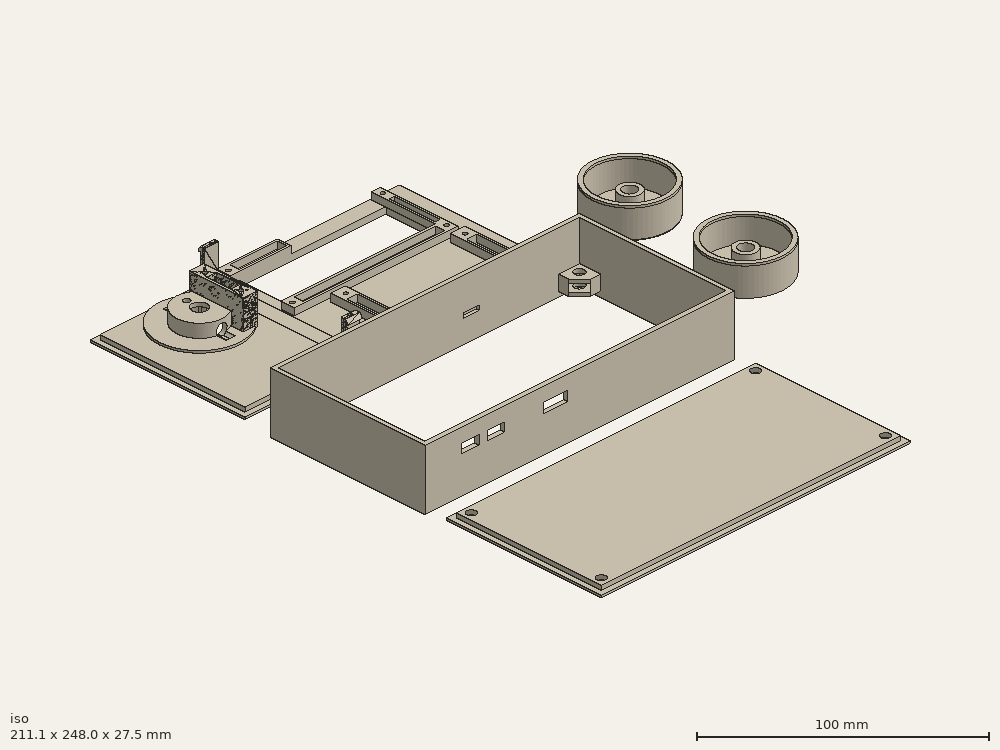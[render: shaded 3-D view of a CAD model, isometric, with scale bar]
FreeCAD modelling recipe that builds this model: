
FCSTD DOCUMENT  (FreeCAD 0.18.4R)
Label: controlbox
License: All rights reserved
LicenseURL: http://en.wikipedia.org/wiki/All_rights_reserved
objects: Part::Extrusion×22, Part::Feature×21, Part::Part2DObjectPython×20, Part::MultiFuse×20, Part::FeaturePython×12, Part::Cut×12, App::DocumentObjectGroup×6
note: 107 computed .brp shape members not serialized (recipe doc carries the construction recipe); baked Part::Feature solids carry a one-line shape summary decoded from their .brp

FEATURE [Part::Feature] Cut279012044
  Placement = pos=(203.269,1.91073,-1) rot=(0,0,1;0rad)
  shape: bbox 150 x 75.1 x 3 mm, 15 faces (baked)
FEATURE [App::DocumentObjectGroup] GrExplode_Slice  label="Exploded Slice"
FEATURE [App::DocumentObjectGroup] GrExplode_Slice001  label="Exploded Slice001"
FEATURE [App::DocumentObjectGroup] GrExplode_Slice002  label="Exploded Slice002"
FEATURE [Part::Part2DObjectPython] Rectangle006  # Draft 2D object (typed FeaturePython)
  ChamferSize = 0
  Columns = 1
  FilletRadius = 0
  Height = 73.0083
  Length = 53.7046
  MakeFace = true
  Placement = pos=(123.234,41.9071,-37.9227) rot=(0.57735,-0.57735,-0.57735;2.0944rad)
  Rows = 1
FEATURE [Part::FeaturePython] Slice003  # WARN: FeaturePython — macro-defined, semantics opaque (R4)
  Mode = 1
  Tolerance = 0
  Tools = -> [Rectangle006]
FEATURE [Part::FeaturePython] Slice003_child0  label="Slice003.0"  # WARN: FeaturePython — macro-defined, semantics opaque (R4)
  Base = -> Slice003
  FilterType = 1
  Invert = false
  OverrideMaxVal = 0
  WindowFrom = 80
  WindowTo = 100
  items = 0
FEATURE [Part::Feature] Face004
  shape: bbox 1.25 x 11.65 x 1.196e-06 mm, 1 faces, 0 solids (baked)
FEATURE [Part::Extrusion] Extrusion048
  Base = -> Face004
  Dir = (-1e-15,1e-16,-4)
  DirMode = 0
  FaceMakerClass = Part::FaceMakerBullseye
  LengthFwd = 0
  LengthRev = 0
  Solid = true
  Symmetric = false
FEATURE [Part::MultiFuse] Fusion
  Shapes = -> [Slice003_child0,Extrusion048]
FEATURE [App::DocumentObjectGroup] GrExplode_Slice003  label="Exploded Slice003"
  Group = -> [Fusion]
FEATURE [Part::Feature] Fusion016003002002002002003007002002020008005003005004002003002008
  shape: bbox 7 x 26 x 14.5 mm, 14 faces (baked)
FEATURE [Part::Feature] Cut279012081006007001  label="Cut279012081006008"
  shape: bbox 22 x 22 x 7 mm, 8 faces (baked)
FEATURE [Part::Part2DObjectPython] Circle022  # Draft 2D object (typed FeaturePython)
  FirstAngle = 0
  LastAngle = 0
  MakeFace = true
  Placement = pos=(117.234,41.9934,4.6) rot=(0,0.707107,0.707107;3.14159rad)
  Radius = 2.6
FEATURE [Part::Extrusion] Extrusion049
  Base = -> Circle022
  Dir = (0,-69.8017,1.55e-14)
  DirMode = 0
  FaceMakerClass = Part::FaceMakerBullseye
  LengthFwd = 0
  LengthRev = 0
  Solid = true
  Symmetric = false
FEATURE [Part::Part2DObjectPython] Circle023  # Draft 2D object (typed FeaturePython)
  FirstAngle = 0
  LastAngle = 0
  MakeFace = true
  Placement = pos=(117.234,22.5909,2) rot=(0,0,1;0rad)
  Radius = 18.3
FEATURE [Part::Part2DObjectPython] Circle024  # Draft 2D object (typed FeaturePython)
  FirstAngle = 0
  LastAngle = 0
  MakeFace = true
  Placement = pos=(117.234,22.5909,2) rot=(1,0,0;3.14159rad)
  Radius = 8
FEATURE [Part::Extrusion] Extrusion050
  Base = -> Circle024
  Dir = (-4.2e-15,-8.8e-15,-36)
  DirMode = 0
  FaceMakerClass = Part::FaceMakerBullseye
  LengthFwd = 0
  LengthRev = 0
  Solid = true
  Symmetric = false
FEATURE [Part::Extrusion] Extrusion051
  Base = -> Circle023
  Dir = (-1e-16,-2e-16,-1)
  DirMode = 0
  FaceMakerClass = Part::FaceMakerBullseye
  LengthFwd = 0
  LengthRev = 0
  Solid = true
  Symmetric = false
FEATURE [Part::Cut] Cut279012081006007003
  Base = -> Extrusion051
  Tool = -> Extrusion050
FEATURE [Part::Cut] Cut279012081006007004
  Base = -> Cut279012081006007001
  Tool = -> Extrusion049
FEATURE [Part::Part2DObjectPython] Circle027  # Draft 2D object (typed FeaturePython)
  FirstAngle = 0
  LastAngle = 0
  MakeFace = true
  Placement = pos=(117.234,22.5909,6) rot=(1,0,0;3.14159rad)
  Radius = 8
  Support = -> [Cut279012081006007004]
FEATURE [Part::Extrusion] Extrusion052
  Base = -> Circle027
  Dir = (1e-16,3e-16,1.2)
  DirMode = 0
  FaceMakerClass = Part::FaceMakerBullseye
  LengthFwd = 0
  LengthRev = 0
  Solid = true
  Symmetric = false
FEATURE [Part::Cut] Cut279012081006007005
  Base = -> Cut279012081006007004
  Tool = -> Extrusion052
FEATURE [Part::Feature] Cut279012081002001  label="Cut279012081006007006"
  shape: bbox 38.81 x 38.81 x 1 mm, 4 faces (baked)
FEATURE [Part::Part2DObjectPython] Circle  # Draft 2D object (typed FeaturePython)
  FirstAngle = 0
  LastAngle = 0
  MakeFace = true
  Placement = pos=(117.217,37.7921,4.5999) rot=(-1,0,0;1.5708rad)
  Radius = 2.7
  Support = -> [Cut279012081002001]
FEATURE [Part::Extrusion] Extrusion053
  Base = -> Circle
  Dir = (-1.9e-15,-30.4017,6.8e-15)
  DirMode = 0
  FaceMakerClass = Part::FaceMakerBullseye
  LengthFwd = 0
  LengthRev = 0
  Solid = true
  Symmetric = false
FEATURE [Part::Cut] Cut279012081006007006  label="Cut279012081006007007"
  Base = -> Cut279012081002001
  Tool = -> Extrusion053
FEATURE [Part::MultiFuse] Fusion016003002002002002003007002002020008005003005004002003002010
  Shapes = -> [Cut279012081006007005,Cut279012081006007006]
FEATURE [Part::MultiFuse] Fusion016003002002002002003007002002020008005003005004002003002011
  Shapes = -> [Fusion016003002002002002003007002002020008005003005004002003002010,Fusion016003002002002002003007002002020008005003005004002003002008]
FEATURE [Part::MultiFuse] Fusion016003002002002002003007002002020008005003005004002003002012
  Shapes = -> [Cut279012081006007003,Fusion016003002002002002003007002002020008005003005004002003002011]
FEATURE [Part::Feature] Cut279012081006003001  label="Cut279012081006007008"
  shape: bbox 150 x 75.1 x 6.5 mm, 76 faces (baked)
FEATURE [Part::MultiFuse] Fusion016003002002002002003007002002020008005003005004002003002013
  Shapes = -> [Cut279012081006003001,Fusion016003002002002002003007002002020008005003005004002003002012]
FEATURE [Part::Feature] Fusion016003002002002002003007002002020008005003005004002003002014001  label="Fusion016003002002002002003007002002020008005003005004002003002015"
  shape: bbox 7 x 4.25 x 15 mm, 9 faces (baked)
FEATURE [Part::MultiFuse] Fusion016003002002002002003007002002020008005003005004002003002014002
  Shapes = -> [Fusion016003002002002002003007002002020008005003005004002003002013,Fusion016003002002002002003007002002020008005003005004002003002014001]
FEATURE [Part::Feature] Fusion016003002002002002003007002002020008005003005004002003002014004001  label="Fusion016003002002002002003007002002020008005003005004002003002014005"
  shape: bbox 7 x 4.25 x 15 mm, 9 faces (baked)
FEATURE [Part::MultiFuse] Fusion016003002002002002003007002002020008005003005004002003002014004002
  Shapes = -> [Fusion016003002002002002003007002002020008005003005004002003002014002,Fusion016003002002002002003007002002020008005003005004002003002014004001]
FEATURE [Part::Feature] Face
  shape: bbox 7 x 2e-07 x 13 mm, 1 faces, 0 solids (baked)
FEATURE [Part::Extrusion] Extrusion061
  Base = -> Face
  Dir = (0,1,0)
  DirMode = 0
  FaceMakerClass = Part::FaceMakerBullseye
  LengthFwd = 0
  LengthRev = 0
  Solid = true
  Symmetric = false
FEATURE [Part::Feature] Face005
  shape: bbox 7 x 1 x 4.243e-07 mm, 1 faces, 0 solids (baked)
FEATURE [Part::Extrusion] Extrusion062
  Base = -> Face005
  Dir = (0,0,-2)
  DirMode = 0
  FaceMakerClass = Part::FaceMakerBullseye
  LengthFwd = 0
  LengthRev = 0
  Solid = true
  Symmetric = false
FEATURE [Part::MultiFuse] Fusion016003002002002002003007002002020008005003005004002003002014004003
  Shapes = -> [Extrusion061,Extrusion062]
FEATURE [Part::Part2DObjectPython] Rectangle012  # Draft 2D object (typed FeaturePython)
  ChamferSize = 0
  Columns = 1
  FilletRadius = 0
  Height = 3
  Length = 3
  MakeFace = true
  Placement = pos=(136.979,-23.4591,2) rot=(0.57735,-0.57735,-0.57735;2.0944rad)
  Rows = 1
FEATURE [Part::Part2DObjectPython] Circle030  # Draft 2D object (typed FeaturePython)
  FirstAngle = 0
  LastAngle = 0
  MakeFace = true
  Placement = pos=(136.979,-23.4591,5) rot=(0.57735,-0.57735,-0.57735;2.0944rad)
  Radius = 3
FEATURE [Part::Extrusion] Extrusion063
  Base = -> Rectangle012
  Dir = (7,0,0)
  DirMode = 0
  FaceMakerClass = Part::FaceMakerBullseye
  LengthFwd = 0
  LengthRev = 0
  Solid = true
  Symmetric = false
FEATURE [Part::Extrusion] Extrusion064
  Base = -> Circle030
  Dir = (7,0,0)
  DirMode = 0
  FaceMakerClass = Part::FaceMakerBullseye
  LengthFwd = 0
  LengthRev = 0
  Solid = true
  Symmetric = false
FEATURE [Part::Cut] Cut279012081006007008  label="Cut279012081006007010"
  Base = -> Extrusion063
  Tool = -> Extrusion064
FEATURE [Part::MultiFuse] Fusion016003002002002002003007002002020008005003005004002003002014004004
  Shapes = -> [Fusion016003002002002002003007002002020008005003005004002003002014004003,Cut279012081006007008]
FEATURE [Part::MultiFuse] Fusion016003002002002002003007002002020008005003005004002003002014004005
  Shapes = -> [Fusion016003002002002002003007002002020008005003005004002003002014004002,Fusion016003002002002002003007002002020008005003005004002003002014004004]
FEATURE [Part::Feature] Face006
  shape: bbox 7 x 2e-07 x 13 mm, 1 faces, 0 solids (baked)
FEATURE [Part::Extrusion] Extrusion065
  Base = -> Face006
  Dir = (0,-1,0)
  DirMode = 0
  FaceMakerClass = Part::FaceMakerBullseye
  LengthFwd = 0
  LengthRev = 0
  Solid = true
  Symmetric = false
FEATURE [Part::Feature] Face007
  shape: bbox 7 x 1 x 4.243e-07 mm, 1 faces, 0 solids (baked)
FEATURE [Part::Extrusion] Extrusion066
  Base = -> Face007
  Dir = (0,0,-2)
  DirMode = 0
  FaceMakerClass = Part::FaceMakerBullseye
  LengthFwd = 0
  LengthRev = 0
  Solid = true
  Symmetric = false
FEATURE [Part::Part2DObjectPython] Rectangle013  # Draft 2D object (typed FeaturePython)
  ChamferSize = 0
  Columns = 1
  FilletRadius = 0
  Height = 3
  Length = 3
  MakeFace = true
  Placement = pos=(136.979,39.9935,2) rot=(0.57735,-0.57735,-0.57735;2.0944rad)
  Rows = 1
  Support = -> [Extrusion066]
FEATURE [Part::Part2DObjectPython] Circle031  # Draft 2D object (typed FeaturePython)
  FirstAngle = 0
  LastAngle = 0
  MakeFace = true
  Placement = pos=(136.979,36.9935,5) rot=(0.57735,-0.57735,-0.57735;2.0944rad)
  Radius = 3
  Support = -> [Extrusion065]
FEATURE [Part::Extrusion] Extrusion067
  Base = -> Rectangle013
  Dir = (7,0,0)
  DirMode = 0
  FaceMakerClass = Part::FaceMakerBullseye
  LengthFwd = 0
  LengthRev = 0
  Solid = true
  Symmetric = false
FEATURE [Part::Extrusion] Extrusion068
  Base = -> Circle031
  Dir = (7,0,0)
  DirMode = 0
  FaceMakerClass = Part::FaceMakerBullseye
  LengthFwd = 0
  LengthRev = 0
  Solid = true
  Symmetric = false
FEATURE [Part::Cut] Cut279012081006007009  label="Cut279012081006007011"
  Base = -> Extrusion067
  Tool = -> Extrusion068
FEATURE [Part::MultiFuse] Fusion016003002002002002003007002002020008005003005004002003002014004006
  Shapes = -> [Cut279012081006007009,Extrusion065]
FEATURE [Part::MultiFuse] Fusion016003002002002002003007002002020008005003005004002003002014004007
  Shapes = -> [Fusion016003002002002002003007002002020008005003005004002003002014004005,Fusion016003002002002002003007002002020008005003005004002003002014004006]
FEATURE [Part::MultiFuse] Fusion016003002002002002003007002002020008005003005004002003002014004008
  Shapes = -> [Fusion016003002002002002003007002002020008005003005004002003002014004007,Extrusion066]
FEATURE [Part::Part2DObjectPython] Rectangle014  # Draft 2D object (typed FeaturePython)
  ChamferSize = 0
  Columns = 1
  FilletRadius = 0
  Height = 70.4526
  Length = 7
  MakeFace = true
  Placement = pos=(136.979,-28.4591,2) rot=(0,0,1;0rad)
  Rows = 1
  Support = -> [Fusion016003002002002002003007002002020008005003005004002003002014004008]
FEATURE [Part::FeaturePython] Slice  # WARN: FeaturePython — macro-defined, semantics opaque (R4)
  Base = -> Fusion016003002002002002003007002002020008005003005004002003002014004008
  Mode = 1
  Tolerance = 0
  Tools = -> [Rectangle014]
FEATURE [Part::FeaturePython] Slice_child0  label="Slice.0"  # WARN: FeaturePython — macro-defined, semantics opaque (R4)
  Base = -> Slice
  FilterType = 1
  Invert = false
  OverrideMaxVal = 0
  WindowFrom = 80
  WindowTo = 100
  items = 0
FEATURE [Part::FeaturePython] Slice_child1001  label="Slice.002"  # WARN: FeaturePython — macro-defined, semantics opaque (R4)
  Base = -> Slice
  FilterType = 1
  Invert = false
  OverrideMaxVal = 0
  WindowFrom = 80
  WindowTo = 100
  items = 1
FEATURE [Part::FeaturePython] Slice_child2  label="Slice.2"  # WARN: FeaturePython — macro-defined, semantics opaque (R4)
  Base = -> Slice
  FilterType = 1
  Invert = false
  OverrideMaxVal = 0
  WindowFrom = 80
  WindowTo = 100
  items = 2
FEATURE [Part::FeaturePython] Slice_child3  label="Slice.3"  # WARN: FeaturePython — macro-defined, semantics opaque (R4)
  Base = -> Slice
  FilterType = 1
  Invert = false
  OverrideMaxVal = 0
  WindowFrom = 80
  WindowTo = 100
  items = 3
FEATURE [Part::FeaturePython] Slice_child4  label="Slice.4"  # WARN: FeaturePython — macro-defined, semantics opaque (R4)
  Base = -> Slice
  FilterType = 1
  Invert = false
  OverrideMaxVal = 0
  WindowFrom = 80
  WindowTo = 100
  items = 4
FEATURE [Part::Feature] Slice_child3001  label="Slice.003"
  shape: bbox 7 x 6.25 x 15 mm, 9 faces (baked)
FEATURE [Part::Feature] Slice_child0001  label="Slice.004"
  shape: bbox 7 x 6.25 x 15 mm, 9 faces (baked)
FEATURE [Part::MultiFuse] Fusion016003002002002002003007002002020008005003005004002003002014004009
  Shapes = -> [Slice_child3001,Slice_child0001]
FEATURE [Part::MultiFuse] Fusion016003002002002002003007002002020008005003005004002003002014004010
  Shapes = -> [Slice_child2,Fusion016003002002002002003007002002020008005003005004002003002014004009]
FEATURE [Part::Part2DObjectPython] Line  # Draft 2D object (typed FeaturePython)
  ChamferSize = 0
  Closed = false
  End = (297.043,-80.6345,11.8)
  FilletRadius = 0
  Length = 12.8
  MakeFace = true
  Placement = pos=(297.043,-80.6345,-1) rot=(0,0,1;0rad)
  Points = (2) [(0,0,0),(0,0,12.8)]
  Start = (297.043,-80.6345,-1)
  Subdivisions = 0
FEATURE [Part::Feature] Fusion016003002002002002003007002002020008005003005004002003002014004011001  label="Fusion016003002002002002003007002002020008005003005004002003002014004012"
  shape: bbox 36 x 36 x 12.8 mm, 11 faces (baked)
FEATURE [Part::Part2DObjectPython] Line001  # Draft 2D object (typed FeaturePython)
  ChamferSize = 0
  Closed = false
  End = (297.043,-24.3987,12.8)
  FilletRadius = 0
  Length = 13.8
  MakeFace = true
  Placement = pos=(297.043,-24.3987,-1) rot=(0,0,1;0rad)
  Points = (2) [(0,0,0),(0,0,13.8)]
  Start = (297.043,-24.3987,-1)
  Subdivisions = 0
FEATURE [Part::Feature] Fusion016003002002002002003007002002020008005003005004002003002014004011002001  label="Fusion016003002002002002003007002002020008005003005004002003002014004011003"
  shape: bbox 36 x 36 x 12.8 mm, 13 faces (baked)
FEATURE [Part::Part2DObjectPython] Rectangle017  # Draft 2D object (typed FeaturePython)
  ChamferSize = 0
  Columns = 1
  FilletRadius = 0
  Height = 70
  Length = 70
  MakeFace = true
  Placement = pos=(230.617,5.027,-0.7) rot=(1,0,0;3.14159rad)
  Rows = 1
  Support = -> [Fusion016003002002002002003007002002020008005003005004002003002014004011001]
FEATURE [Part::FeaturePython] Slice004  # WARN: FeaturePython — macro-defined, semantics opaque (R4)
  Base = -> Fusion016003002002002002003007002002020008005003005004002003002014004011002001
  Mode = 1
  Tolerance = 0
  Tools = -> [Rectangle017]
FEATURE [Part::FeaturePython] Slice004_child0  label="Slice004.0"  # WARN: FeaturePython — macro-defined, semantics opaque (R4)
  Base = -> Slice004
  FilterType = 1
  Invert = false
  OverrideMaxVal = 0
  WindowFrom = 80
  WindowTo = 100
  items = 0
FEATURE [Part::FeaturePython] Slice004_child1  label="Slice004.1"  # WARN: FeaturePython — macro-defined, semantics opaque (R4)
  Base = -> Slice004
  FilterType = 1
  Invert = false
  OverrideMaxVal = 0
  WindowFrom = 80
  WindowTo = 100
  items = 1
FEATURE [Part::FeaturePython] Slice004_child2  label="Slice004.2"  # WARN: FeaturePython — macro-defined, semantics opaque (R4)
  Base = -> Slice004
  FilterType = 1
  Invert = false
  OverrideMaxVal = 0
  WindowFrom = 80
  WindowTo = 100
  items = 2
FEATURE [Part::Part2DObjectPython] Circle032  # Draft 2D object (typed FeaturePython)
  FirstAngle = 0
  LastAngle = 0
  MakeFace = true
  Placement = pos=(279.043,-24.3987,-0.7) rot=(1,0,0;3.14159rad)
  Radius = 15
FEATURE [Part::Extrusion] Extrusion
  Base = -> Circle032
  Dir = (0,0,26.1259)
  DirMode = 0
  FaceMakerClass = Part::FaceMakerBullseye
  LengthFwd = 0
  LengthRev = 0
  Solid = true
  Symmetric = false
FEATURE [Part::Part2DObjectPython] Circle033  # Draft 2D object (typed FeaturePython)
  FirstAngle = 0
  LastAngle = 0
  MakeFace = true
  Placement = pos=(279.043,-24.3987,-0.7) rot=(1,0,0;3.14159rad)
  Radius = 16
  Support = -> [Slice004_child2]
FEATURE [Part::Extrusion] Extrusion069
  Base = -> Circle033
  Dir = (0,0,26.1259)
  DirMode = 0
  FaceMakerClass = Part::FaceMakerBullseye
  LengthFwd = 0
  LengthRev = 0
  Solid = true
  Symmetric = false
FEATURE [Part::Cut] Cut
  Base = -> Extrusion069
  Tool = -> Extrusion
FEATURE [Part::Cut] Cut279012081006007010  label="Cut279012081006007012"
  Base = -> Slice004_child2
  Tool = -> Cut
FEATURE [Part::Part2DObjectPython] Circle035  # Draft 2D object (typed FeaturePython)
  FirstAngle = 0
  LastAngle = 0
  MakeFace = true
  Placement = pos=(279.043,-24.3987,-0.7) rot=(1,0,0;3.14159rad)
  Radius = 15
  Support = -> [Cut279012081006007010]
FEATURE [Part::Extrusion] Extrusion071
  Base = -> Circle035
  Dir = (0,0,62.2869)
  DirMode = 0
  FaceMakerClass = Part::FaceMakerBullseye
  LengthFwd = 0
  LengthRev = 0
  Solid = true
  Symmetric = false
FEATURE [Part::Part2DObjectPython] Circle036  # Draft 2D object (typed FeaturePython)
  FirstAngle = 0
  LastAngle = 0
  MakeFace = true
  Placement = pos=(279.043,-24.3987,-0.7) rot=(1,0,0;3.14159rad)
  Radius = 14
  Support = -> [Cut279012081006007010]
FEATURE [Part::Extrusion] Extrusion072
  Base = -> Circle036
  Dir = (0,0,62.2869)
  DirMode = 0
  FaceMakerClass = Part::FaceMakerBullseye
  LengthFwd = 0
  LengthRev = 0
  Solid = true
  Symmetric = false
FEATURE [Part::Cut] Cut279012081006007011  label="Cut279012081006007013"
  Base = -> Extrusion071
  Tool = -> Extrusion072
FEATURE [Part::Cut] Cut279012081006007012  label="Cut279012081006007014"
  Base = -> Cut279012081006007010
  Tool = -> Cut279012081006007011
FEATURE [Part::MultiFuse] Fusion016003002002002002003007002002020008005003005004002003002014004011002002
  Shapes = -> [Slice004_child1,Slice004_child0]
FEATURE [Part::MultiFuse] Fusion016003002002002002003007002002020008005003005004002003002014004011002003
  Shapes = -> [Cut279012081006007012,Fusion016003002002002002003007002002020008005003005004002003002014004011002002]
FEATURE [Part::Feature] Face008
  shape: bbox 1.25 x 10.58 x 1.691e-06 mm, 1 faces, 0 solids (baked)
FEATURE [Part::Extrusion] Extrusion073
  Base = -> Face008
  Dir = (1e-16,0,1.2)
  DirMode = 0
  FaceMakerClass = Part::FaceMakerBullseye
  LengthFwd = 0
  LengthRev = 0
  Solid = true
  Symmetric = false
FEATURE [Part::Cut] Cut279012081006007013  label="Cut279012081006007015"
  Base = -> Fusion016003002002002002003007002002020008005003005004002003002014004010
  Tool = -> Extrusion073
FEATURE [Part::MultiFuse] Fusion004002009
  Shapes = -> [Slice_child0001]
FEATURE [Part::Part2DObjectPython] Line005  # Draft 2D object (typed FeaturePython)
  ChamferSize = 0
  Closed = false
  End = (125.234,22.5909,1)
  FilletRadius = 0
  Length = 8
  MakeFace = true
  Placement = pos=(117.234,22.5909,1) rot=(1,0,0;3.14159rad)
  Points = (2) [(0,0,0),(8,0,1.11022e-15)]
  Start = (117.234,22.5909,1)
  Subdivisions = 0
  Support = -> [Cut279012081006007013]
FEATURE [Part::Part2DObjectPython] Line006  # Draft 2D object (typed FeaturePython)
  ChamferSize = 0
  Closed = false
  End = (117.234,22.5909,9)
  FilletRadius = 0
  Length = 3.5
  MakeFace = true
  Placement = pos=(120.734,22.5909,9) rot=(0,0,1;0rad)
  Points = (2) [(0,0,0),(-3.5,0,0)]
  Start = (120.734,22.5909,9)
  Subdivisions = 0
  Support = -> [Cut279012081006007013]
FEATURE [Part::Feature] Face009
  Placement = pos=(117.234,22.5909,-47.3018) rot=(1,0,0;3.14159rad)
  shape: bbox 18 x 18 x 2e-07 mm, 1 faces, 0 solids (baked)
FEATURE [Part::Feature] Face010
  Placement = pos=(0,56.2358,3) rot=(0,0,1;0rad)
  shape: bbox 36 x 36 x 2e-07 mm, 1 faces, 0 solids (baked)
FEATURE [Part::Feature] Face011
  Placement = pos=(0,0,3) rot=(0,0,1;0rad)
  shape: bbox 36 x 36 x 2e-07 mm, 1 faces, 0 solids (baked)
FEATURE [Part::Extrusion] Extrusion076
  Base = -> Face009
  Dir = (0,0,54.5018)
  DirMode = 0
  FaceMakerClass = Part::FaceMakerBullseye
  LengthFwd = 0
  LengthRev = 0
  Solid = true
  Symmetric = false
FEATURE [Part::Cut] Cut279012081006007014  label="Cut279012081006007016"
  Base = -> Cut279012081006007013
  Tool = -> Extrusion076
FEATURE [App::DocumentObjectGroup] GrExplode_Slice004  label="Exploded Slice004"
  Group = -> [Slice_child0,Slice_child1001,Slice_child3,Slice_child4,Cut279012081006007014]
FEATURE [Part::Extrusion] Extrusion077
  Base = -> Face010
  Dir = (0,0,1)
  DirMode = 0
  FaceMakerClass = Part::FaceMakerBullseye
  LengthFwd = 0
  LengthRev = 0
  Solid = true
  Symmetric = false
FEATURE [Part::MultiFuse] Fusion016003002002002002003007002002020008005003005004002003002014004011002004
  Shapes = -> [Fusion016003002002002002003007002002020008005003005004002003002014004011002003,Extrusion077]
FEATURE [App::DocumentObjectGroup] GrExplode_Slice004001  label="Exploded Slice005"
  Group = -> [Fusion016003002002002002003007002002020008005003005004002003002014004011002004]
FEATURE [Part::Feature] Face012
  shape: bbox 4.35 x 3e-07 x 1 mm, 1 faces, 0 solids (baked)
FEATURE [Part::Extrusion] Extrusion078
  Base = -> Face011
  Dir = (0,0,1)
  DirMode = 0
  FaceMakerClass = Part::FaceMakerBullseye
  LengthFwd = 0
  LengthRev = 0
  Solid = true
  Symmetric = false
FEATURE [Part::MultiFuse] Fusion016003002002002002003007002002020008005003005004002003002014004011002005
  Shapes = -> [Fusion016003002002002002003007002002020008005003005004002003002014004011001,Extrusion078]
